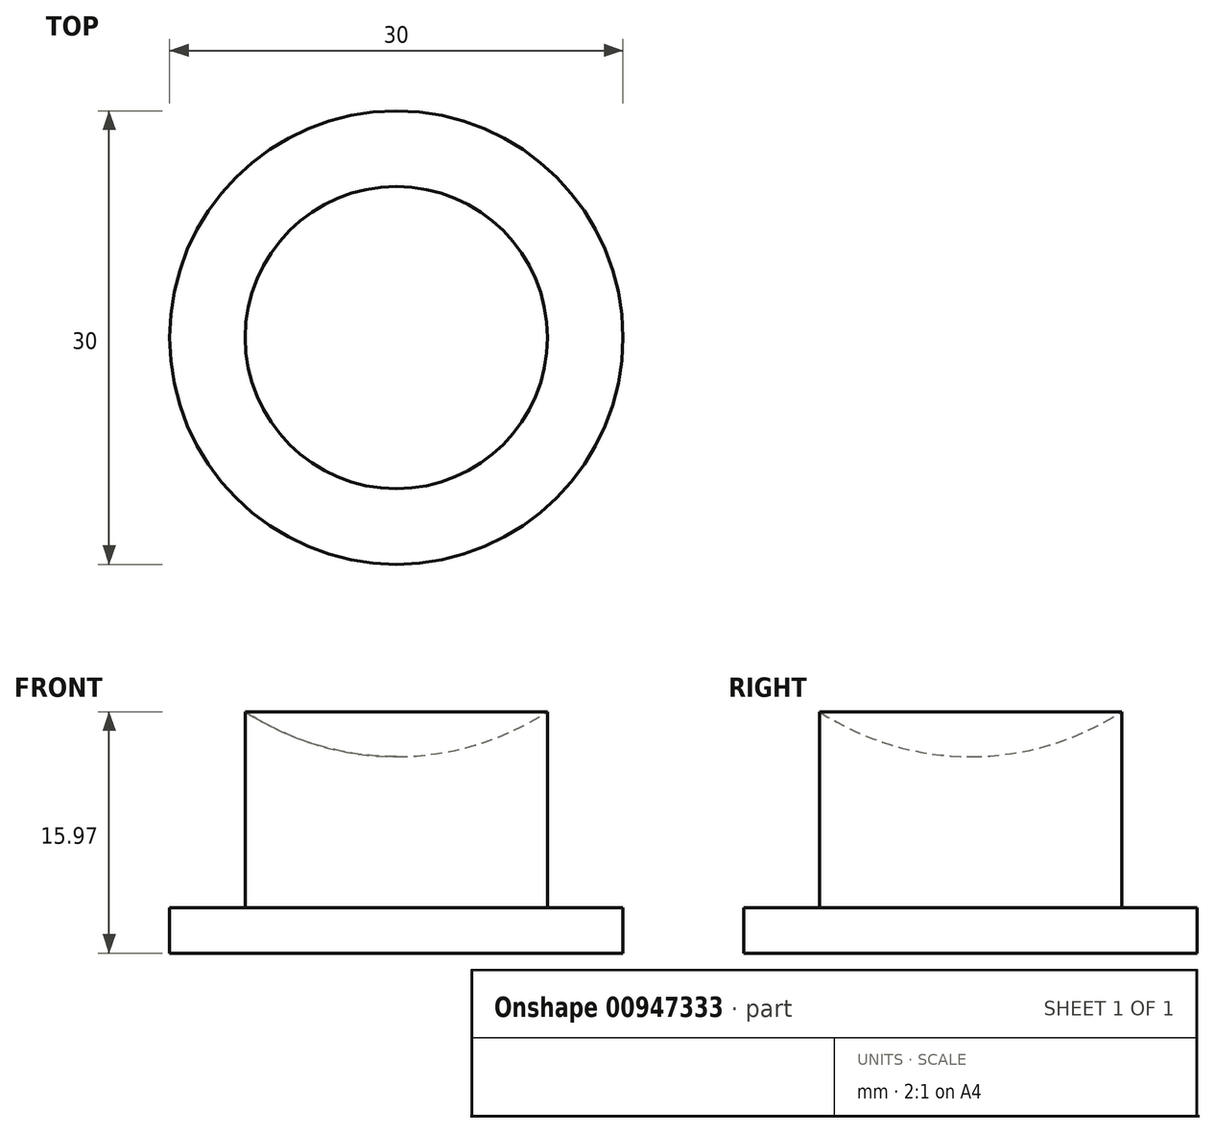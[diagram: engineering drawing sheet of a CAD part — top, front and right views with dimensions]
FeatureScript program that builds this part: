
annotation { "Feature Type Name" : "Feature", "Feature Type Description" : "" }
export const myFeature = defineFeature(function(context is Context, id is Id, definition is map)
    precondition{}
    {
        {
            var Q0;
            Q0=qCreatedBy(makeId("Front.planeOp"),FACE);
            var sketch = newSketch(context, id + "F0", { "sketchPlane" : qUnion([Q0])});
            skLineSegment(sketch, "E0.bottom", {"start": v(0, 0) * mm, "end": v(-15, 0) * mm});
            skLineSegment(sketch, "E0.top", {"start": v(0, 3) * mm, "end": v(-15, 3) * mm});
            skLineSegment(sketch, "E0.left", {"start": v(0, 0) * mm, "end": v(0, 3) * mm});
            skLineSegment(sketch, "E0.right", {"start": v(-15, 0) * mm, "end": v(-15, 3) * mm});
            skLineSegment(sketch, "E1", {"start": v(-10, 3) * mm, "end": v(-10, 15.97) * mm});
            skLineSegment(sketch, "E2", {"start": v(0, 13) * mm, "end": v(0, 3) * mm});
            skArc(sketch, "E3", {"start": v(0, 13) * mm, "mid": v(-5.22, 13.76) * mm, "end": v(-10, 15.97) * mm});
            skSolve(sketch);
        }
        {
            var Q0;
            Q0 = qSketchRegion(id + "F0", true);
            var Q1;
            Q1=sQuery(id+"F0.wireOp",EDGE,"E2");
            revolve(context, id + "F1", {"surfaceOperationType" : NewSurfaceOperationType.NEW, "entities" : qUnion([Q0]), "axis" : qUnion([Q1]), "revolveType" : RevolveType.FULL});
        }
    });
